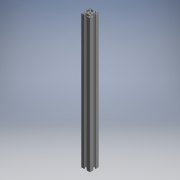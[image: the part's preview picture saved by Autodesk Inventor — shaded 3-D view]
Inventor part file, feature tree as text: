
AUTODESK INVENTOR PART (.ipt)
format: ipt  version: 2017.3 (Build 213256000, 256)  size: 210,432 bytes
history: native  units: mm (DEFAULTED — no unit token found)
features: other x21, sketch x3, hole x2, extrude x1, pattern_linear x1
ambient origin geometry x8: Origin, YZ Plane, XZ Plane, XY Plane, X Axis, Y Axis, Z Axis, Center Point
bodies: Solid1 (feature_tree)
feature tree (28):
  extrude  "Extrusion1"  Depth=440.0mm
  hole  "Hole1"  [1 undecoded]
  hole  "Hole2"  [1 undecoded]
  pattern_linear  "Rectangular Pattern1"  [2 undecoded]
  other  "C1_XY"
  other  "C1_YZ"
  other  "C1_ZX"
  other  "C1_X"
  other  "C1_Y"
  other  "C1_Z"
  other  "C1_Center"
  other  "to_frame_cap1_XY"
  other  "to_frame_cap1_YZ"
  other  "to_frame_cap1_ZX"
  other  "to_frame_cap1_X"
  other  "to_frame_cap1_Y"
  other  "to_frame_cap1_Z"
  other  "to_frame_cap1_Center"
  other  "to_frame_cap2_XY"
  other  "to_frame_cap2_YZ"
  other  "to_frame_cap2_ZX"
  other  "to_frame_cap2_X"
  other  "to_frame_cap2_Y"
  other  "to_frame_cap2_Z"
  other  "to_frame_cap2_Center"
  sketch  "Sketch_1"  dims[d0=440.0mm d1=0.0mm]
  sketch  "Sketch2"  dims[d2=6.8mm d3=6.0mm d4=4.0mm d5=2.0mm d6=90.0deg d7=440.0mm d8=0.0mm]
  sketch  "Sketch3"  dims[d9=4.2mm d10=6.0mm d11=4.0mm d12=2.0mm d13=90.0deg d14=440.0mm d15=0.0mm d16=20.0mm d18=23.2mm d19=20.0mm d21=23.2mm d22=0.0mm d23=0.0mm d24=0.0mm]
note: 4 required parameter values undecoded (feature->parameter linkage not recoverable at this tier; creation-order binding heuristic only, values carry confidence <= 0.55)
